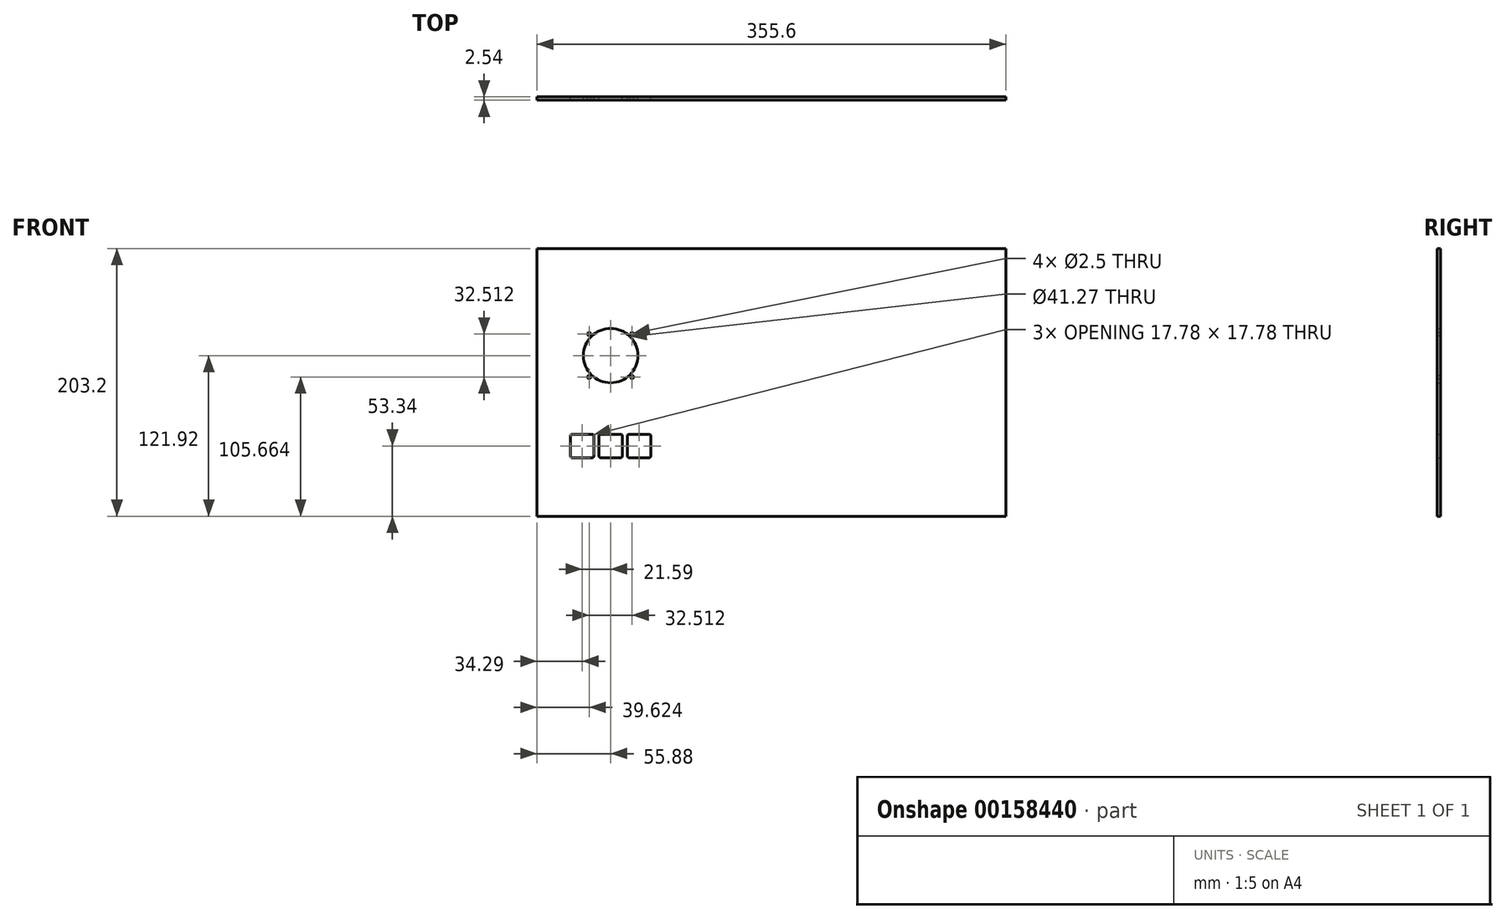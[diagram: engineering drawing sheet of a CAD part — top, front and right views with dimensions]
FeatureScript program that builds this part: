
annotation { "Feature Type Name" : "Feature", "Feature Type Description" : "" }
export const myFeature = defineFeature(function(context is Context, id is Id, definition is map)
    precondition{}
    {
        {
            var Q0;
            Q0=qCreatedBy(makeId("Front.planeOp"),FACE);
            var sketch = newSketch(context, id + "F0", { "sketchPlane" : qUnion([Q0])});
            skLineSegment(sketch, "E0.bottom", {"start": v(0, 0) * mm, "end": v(355.6, 0) * mm});
            skLineSegment(sketch, "E0.top", {"start": v(0, 203.2) * mm, "end": v(355.6, 203.2) * mm});
            skLineSegment(sketch, "E0.left", {"start": v(0, 0) * mm, "end": v(0, 203.2) * mm});
            skLineSegment(sketch, "E0.right", {"start": v(355.6, 0) * mm, "end": v(355.6, 203.2) * mm});
            skLineSegment(sketch, "E1", {"start": v(106.68, 203.2) * mm, "end": v(106.68, 0) * mm, "construction": true});
            skLineSegment(sketch, "E2", {"start": v(5.08, 203.2) * mm, "end": v(5.08, 0) * mm, "construction": true});
            skCircle(sketch, "E3", {"center": v(55.88, 121.92) * mm, "radius": 20.64 * mm});
            skLineSegment(sketch, "E4", {"start": v(5.08, 177.8) * mm, "end": v(106.68, 177.8) * mm, "construction": true});
            skLineSegment(sketch, "E5", {"start": v(55.88, 76.2) * mm, "end": v(55.88, 167.64) * mm, "construction": true});
            skLineSegment(sketch, "E6", {"start": v(5.08, 76.2) * mm, "end": v(106.68, 76.2) * mm, "construction": true});
            skCircle(sketch, "E7", {"center": v(55.88, 121.92) * mm, "radius": 26.54 * mm, "construction": true});
            skCircle(sketch, "E8", {"center": v(39.62, 138.18) * mm, "radius": 1.25 * mm});
            skCircle(sketch, "E9.1.0", {"center": v(39.62, 105.66) * mm, "radius": 1.25 * mm});
            skCircle(sketch, "E9.2.0", {"center": v(72.14, 105.66) * mm, "radius": 1.25 * mm});
            skCircle(sketch, "E9.3.0", {"center": v(72.14, 138.18) * mm, "radius": 1.25 * mm});
            skLineSegment(sketch, "E10", {"start": v(5.08, 167.64) * mm, "end": v(106.68, 167.64) * mm, "construction": true});
            skLineSegment(sketch, "E11", {"start": v(5.08, 198.12) * mm, "end": v(106.68, 198.12) * mm, "construction": true});
            skLineSegment(sketch, "E12", {"start": v(5.08, 66.04) * mm, "end": v(106.68, 66.04) * mm, "construction": true});
            skLineSegment(sketch, "E13", {"start": v(5.08, 29.2) * mm, "end": v(106.68, 29.21) * mm, "construction": true});
            skLineSegment(sketch, "E14", {"start": v(5.08, 53.34) * mm, "end": v(106.68, 53.34) * mm, "construction": true});
            skLineSegment(sketch, "E15", {"start": v(5.08, 41.9) * mm, "end": v(106.68, 41.91) * mm, "construction": true});
            skLineSegment(sketch, "E16", {"start": v(34.29, 66.04) * mm, "end": v(34.29, 29.2) * mm, "construction": true});
            skLineSegment(sketch, "E17", {"start": v(55.88, 66.04) * mm, "end": v(55.88, 29.2) * mm, "construction": true});
            skLineSegment(sketch, "E18.MirrorCS", {"start": v(77.47, 66.04) * mm, "end": v(77.47, 29.21) * mm, "construction": true});
            skPoint(sketch, "E19", {"position": v(34.29, 53.34) * mm});
            skPoint(sketch, "E20", {"position": v(55.88, 53.34) * mm});
            skPoint(sketch, "E21", {"position": v(77.47, 53.34) * mm});
            skLineSegment(sketch, "E22.bottom", {"start": v(41.9, 62.23) * mm, "end": v(26.67, 62.23) * mm});
            skLineSegment(sketch, "E22.top", {"start": v(41.9, 44.45) * mm, "end": v(26.67, 44.45) * mm});
            skLineSegment(sketch, "E22.left", {"start": v(43.18, 60.96) * mm, "end": v(43.18, 45.72) * mm});
            skLineSegment(sketch, "E22.right", {"start": v(25.4, 60.96) * mm, "end": v(25.4, 45.72) * mm});
            skLineSegment(sketch, "E23.bottom", {"start": v(85.09, 62.23) * mm, "end": v(69.85, 62.23) * mm});
            skLineSegment(sketch, "E23.top", {"start": v(85.09, 44.45) * mm, "end": v(69.85, 44.45) * mm});
            skLineSegment(sketch, "E23.left", {"start": v(86.36, 60.96) * mm, "end": v(86.36, 45.72) * mm});
            skLineSegment(sketch, "E23.right", {"start": v(68.58, 60.96) * mm, "end": v(68.58, 45.72) * mm});
            skPoint(sketch, "E24.visualSharp", {"position": v(25.4, 62.23) * mm});
            skArc(sketch, "E24.filletArc", {"start": v(26.67, 62.23) * mm, "mid": v(25.77, 61.86) * mm, "end": v(25.4, 60.96) * mm});
            skPoint(sketch, "E25.visualSharp", {"position": v(43.18, 62.23) * mm});
            skArc(sketch, "E25.filletArc", {"start": v(43.18, 60.96) * mm, "mid": v(42.8, 61.86) * mm, "end": v(41.9, 62.23) * mm});
            skPoint(sketch, "E26.visualSharp", {"position": v(43.18, 44.45) * mm});
            skArc(sketch, "E26.filletArc", {"start": v(41.9, 44.45) * mm, "mid": v(42.8, 44.82) * mm, "end": v(43.18, 45.72) * mm});
            skPoint(sketch, "E27.visualSharp", {"position": v(25.4, 44.45) * mm});
            skArc(sketch, "E27.filletArc", {"start": v(25.4, 45.72) * mm, "mid": v(25.77, 44.82) * mm, "end": v(26.67, 44.45) * mm});
            skPoint(sketch, "E28.visualSharp", {"position": v(68.58, 44.45) * mm});
            skArc(sketch, "E28.filletArc", {"start": v(68.58, 45.72) * mm, "mid": v(68.95, 44.82) * mm, "end": v(69.85, 44.45) * mm});
            skPoint(sketch, "E29.visualSharp", {"position": v(68.58, 62.23) * mm});
            skArc(sketch, "E29.filletArc", {"start": v(69.85, 62.23) * mm, "mid": v(68.95, 61.86) * mm, "end": v(68.58, 60.96) * mm});
            skPoint(sketch, "E30.visualSharp", {"position": v(86.36, 62.23) * mm});
            skArc(sketch, "E30.filletArc", {"start": v(86.36, 60.96) * mm, "mid": v(85.99, 61.86) * mm, "end": v(85.09, 62.23) * mm});
            skPoint(sketch, "E31.visualSharp", {"position": v(86.36, 44.45) * mm});
            skArc(sketch, "E31.filletArc", {"start": v(85.09, 44.45) * mm, "mid": v(85.99, 44.82) * mm, "end": v(86.36, 45.72) * mm});
            skLineSegment(sketch, "E32.bottom", {"start": v(63.5, 62.23) * mm, "end": v(48.26, 62.23) * mm});
            skLineSegment(sketch, "E32.top", {"start": v(63.5, 44.45) * mm, "end": v(48.26, 44.45) * mm});
            skLineSegment(sketch, "E32.left", {"start": v(64.77, 60.96) * mm, "end": v(64.77, 45.72) * mm});
            skLineSegment(sketch, "E32.right", {"start": v(46.99, 60.96) * mm, "end": v(46.99, 45.72) * mm});
            skPoint(sketch, "E33.visualSharp", {"position": v(46.99, 62.23) * mm});
            skArc(sketch, "E33.filletArc", {"start": v(48.26, 62.23) * mm, "mid": v(47.36, 61.86) * mm, "end": v(46.99, 60.96) * mm});
            skPoint(sketch, "E34.visualSharp", {"position": v(64.77, 62.23) * mm});
            skArc(sketch, "E34.filletArc", {"start": v(64.77, 60.96) * mm, "mid": v(64.4, 61.86) * mm, "end": v(63.5, 62.23) * mm});
            skPoint(sketch, "E35.visualSharp", {"position": v(64.77, 44.45) * mm});
            skArc(sketch, "E35.filletArc", {"start": v(63.5, 44.45) * mm, "mid": v(64.4, 44.82) * mm, "end": v(64.77, 45.72) * mm});
            skPoint(sketch, "E36.visualSharp", {"position": v(46.99, 44.45) * mm});
            skArc(sketch, "E36.filletArc", {"start": v(46.99, 45.72) * mm, "mid": v(47.36, 44.82) * mm, "end": v(48.26, 44.45) * mm});
            skPoint(sketch, "E37", {"position": v(34.29, 41.9) * mm});
            skPoint(sketch, "E38", {"position": v(55.88, 41.9) * mm});
            skPoint(sketch, "E39", {"position": v(77.47, 41.91) * mm});
            skSolve(sketch);
        }
        {
            var Q0;
            Q0 = qSketchRegion(id + "F0", true);
            extrude(context, id + "F1", {"entities" : qUnion([Q0]), "depth" : 2.54 * mm});
        }
    });
